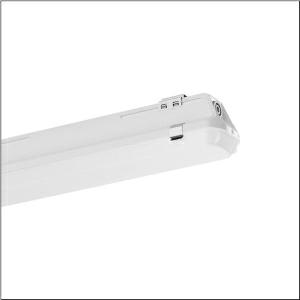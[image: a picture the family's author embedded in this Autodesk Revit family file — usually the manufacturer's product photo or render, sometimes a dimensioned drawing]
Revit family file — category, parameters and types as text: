
# Revit family: monsun_r__11_chemical_51fp30dp460h_97dc
name_source: partatom
category: Lighting Fixtures
units: mm (PartAtom-declared; Revit-internal decimal feet)

## family parameters
Cut with Voids When Loaded = No
Host = Face
Light Source = No
Part Type = Normal
Room Calculation Point = No
Round Connector Dimension = Use Diameter
Shared = No

## types (1)
- --- (1 x LED, 5730 lm, 34.6 W, 4000K)
    Apparent Load = 35 VA
    CIE Flux Codes = 48 77 93 95 100
    Color Rendering = 80
    Color Temperature = 4000K
    Default Elevation = 1800 mm
    Description = Monsun® 11 chemical, damp-proof luminaire, chain hanger, primary optical cover: enclosure, of PA, light emission: direct distribution, primary light characteristic: symmetric, installation type: suspended mounting, surface-mounted, horizontal mounting, vertical mounting, LED, rated luminous flux: 5.730lm, luminous efficacy: 166lm/W, light colour: 840, colour temperature: 4000K, control gear: ECG DALI, with terminal, 5-pole, max. 2.5mm², mains connection: 220..240V, AC, 50/60Hz, rated input power: 35W, luminaire housing, of glass-fibre reinforced polyester, uncoated, bright grey, incl. chain hanger, length: 1.590mm, width: 90mm, height: 88mm, clip for enclosure, of stainless steel (V2A), ceiling mounting element, of stainless steel (V2A), chain hanger, of stainless steel (V2A), protection rating (complete): IP66, insulation class (complete): insulation class I (protective earthing), certification: CE, ENEC, VDE, UKCA, protection symbol: D, impact resistance: IK08, permissible operating ambient temperature: -25..+40°C, standard: EN 50419, EN 60598-2-1, no direct snow, no direct sun, no direct rain, for indoor or canopied outdoor use, corresponds to IFS (International Featured Standards) requirements for safety and quality in the food industry, contact your sales advisor before using the luminaires in applications with unclear chemical exposure, large temperature fluctuations or condensation-forming humidity, LABS conformity tested according to VDMA 24364:2018-05, packaging unit: 1 piece
    Height = 89 mm
    Lamp = 1 x LED
    Lamp Light Flux = 5730 lm
    Lamp Power = 34.6 W
    Lamp count = 1
    Length = 1590 mm
    Luminous efficacy = 166 lm/W
    Manufacturer = Siteco
    ModVariant = No
    Model = 51FP30DP460H
    Mounting Place = Ceiling
    Mounting Type = Surface mounted
    Number of Poles = 1
    OnlyDefault = Yes
    Power Factor = 1
    Product Name = Monsun® 11 chemical
    Product group = damp-proof luminaire
    ProductGroupID = 301
    Protection Class = Protection class I
    Protection Degree = IP 66
    RLX_Detail_Level = 1
    RLX_Emergency_Light_Flux = 0 lm
    RLX_Emergency_Type = 0
    RLX_Emergency_Type_DB = No
    RlxData = <blob elided: 92373 chars, md5=a6442225>
    Socket = socket
    Standby Power = 0 W
    System Light Flux = 5730 lm
    System Power = 35 W
    Type Comments = factory setting: luminous flux: 100 % | dim-lin: 254 | 232 mA
    Type Image = l_1004748.jpg
    URL = http://relux.com
    VarID = @adj_157137
    Voltage = 0 V
    Weight = 0.00 kg
    Width = 90 mm

## geometry (parser evidence)
native form markers: Blend x4, Sweep x15
no freeform markers — native parametric forms only
